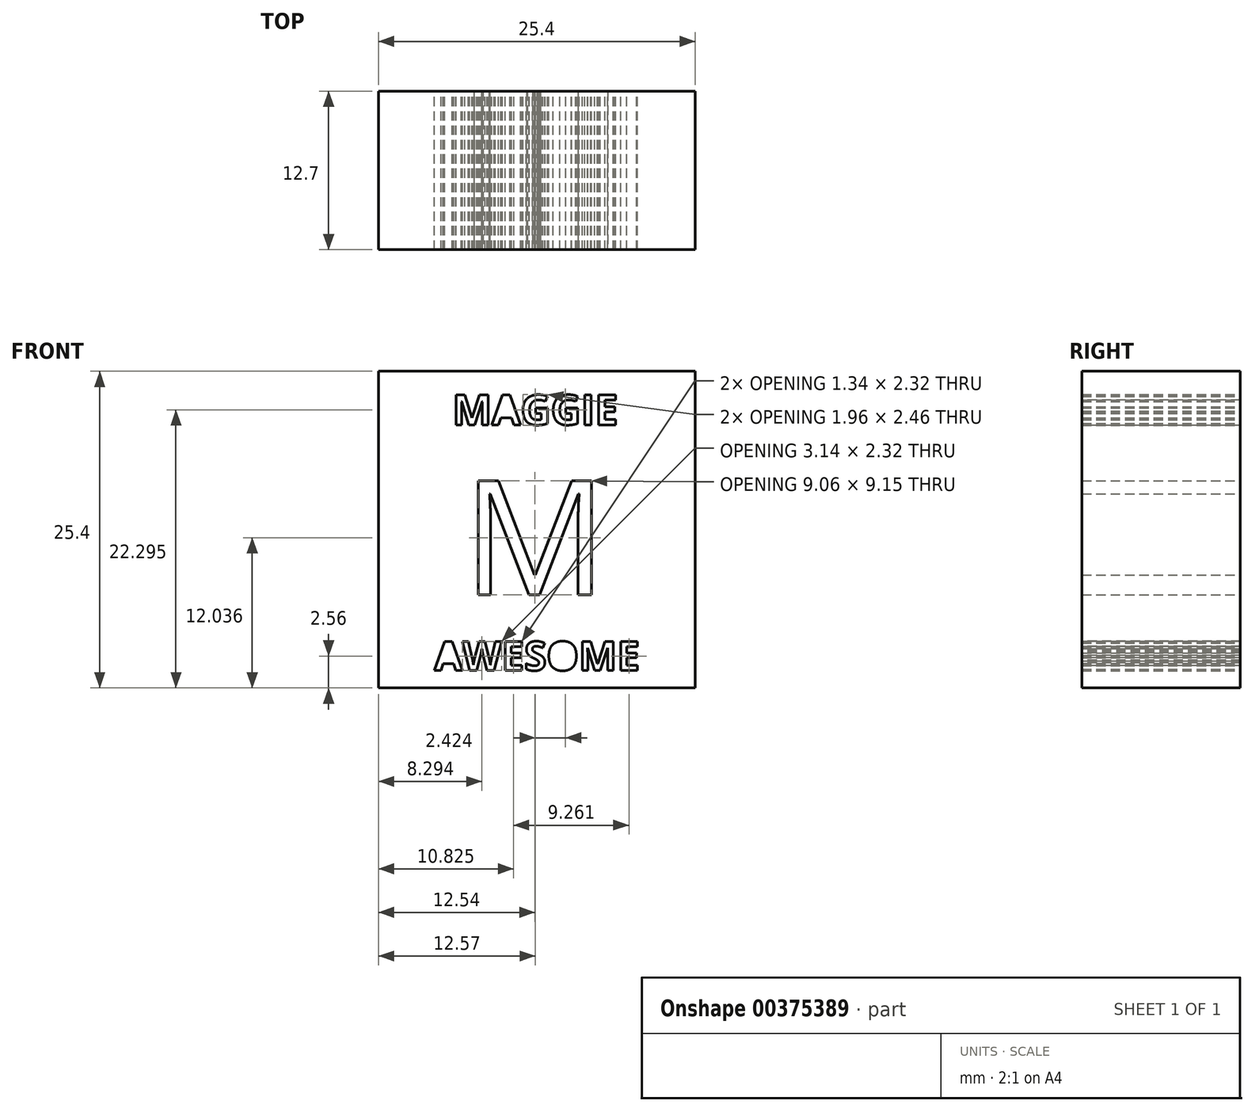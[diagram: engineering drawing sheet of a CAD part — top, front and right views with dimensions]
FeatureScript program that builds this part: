
annotation { "Feature Type Name" : "Feature", "Feature Type Description" : "" }
export const myFeature = defineFeature(function(context is Context, id is Id, definition is map)
    precondition{}
    {
        {
            var Q0;
            Q0=qCreatedBy(makeId("Front.planeOp"),FACE);
            var sketch = newSketch(context, id + "F0", { "sketchPlane" : qUnion([Q0])});
            skLineSegment(sketch, "E0.bottom", {"start": v(-12.7, 12.7) * mm, "end": v(12.7, 12.7) * mm});
            skLineSegment(sketch, "E0.top", {"start": v(-12.7, -12.7) * mm, "end": v(12.7, -12.7) * mm});
            skLineSegment(sketch, "E0.left", {"start": v(-12.7, 12.7) * mm, "end": v(-12.7, -12.7) * mm});
            skLineSegment(sketch, "E0.right", {"start": v(12.7, 12.7) * mm, "end": v(12.7, -12.7) * mm});
            skPoint(sketch, "E0.middle", {"position": v(0, 0) * mm});
            skText(sketch, "E1", { "text": "MAGGIE", "fontName": "OpenSans-Bold.ttf"});
            skText(sketch, "E2", { "text": "AWESOME", "fontName": "OpenSans-Bold.ttf"});
            skText(sketch, "E3", { "text": "M", "fontName": "OpenSans-Regular.ttf"});
            const initialGuessF0  = {"E1": [-0.00677, 0.0084, 1, 0, 0.00241], "E2": [-0.00822, -0.0113, 1, 0, 0.00234], "E3": [-0.00595, -0.00524, 1, 0, 0.00923]};
            skSetInitialGuess(sketch, initialGuessF0);
            skSolve(sketch);
        }
        {
            var Q0;
            Q0 = qSketchRegion(id + "F0", true);
            extrude(context, id + "F1", {"entities" : qUnion([Q0]), "depth" : 12.7 * mm});
        }
    });
